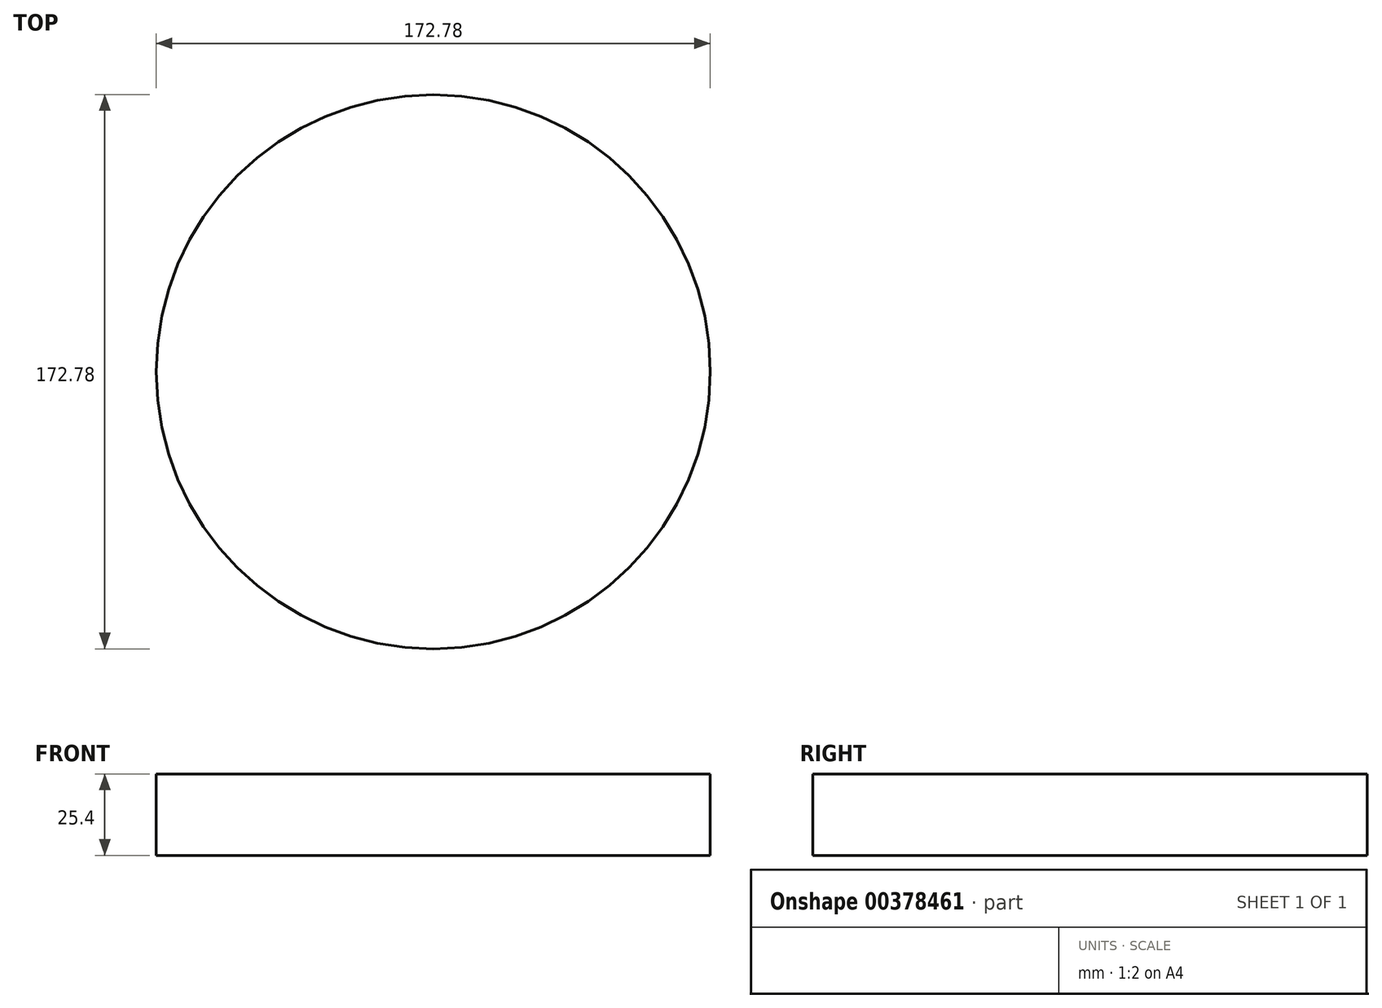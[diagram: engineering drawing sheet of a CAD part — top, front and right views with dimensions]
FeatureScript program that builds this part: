
annotation { "Feature Type Name" : "Feature", "Feature Type Description" : "" }
export const myFeature = defineFeature(function(context is Context, id is Id, definition is map)
    precondition{}
    {
        {
            var Q0;
            Q0=qCreatedBy(makeId("Top.planeOp"),FACE);
            var sketch = newSketch(context, id + "F0", { "sketchPlane" : qUnion([Q0])});
            skCircle(sketch, "E0", {"center": v(0, 0) * mm, "radius": 86.39 * mm});
            skSolve(sketch);
        }
        {
            var Q0;
            Q0=makeQuery(id+"F0.imprint","IMPRINT",FACE,{"disambiguationData":[TD([[makeQuery(id+"F0.imprint","IMPRINT",EDGE,{"derivedFrom":sQuery(id+"F0.wireOp",EDGE,"E0")}),1.0]])]});
            var sketch = newSketch(context, id + "F1", { "sketchPlane" : qUnion([Q0])});
            skCircle(sketch, "E1", {"center": v(0, 0) * mm, "radius": 61.76 * mm});
            skSolve(sketch);
        }
        {
            var Q0;
            Q0=makeQuery(id+"F1.imprint","IMPRINT",FACE,{"disambiguationData":[TD([[makeQuery(id+"F1.imprint","IMPRINT",EDGE,{"derivedFrom":sQuery(id+"F1.wireOp",EDGE,"E1")}),1.0]])]});
            var Q1;
            Q1=makeQuery(id+"F1.imprint","IMPRINT",FACE,{"disambiguationData":[TD([[makeQuery(id+"F1.imprint","IMPRINT",EDGE,{"derivedFrom":sQuery(id+"F1.wireOp",EDGE,"E1")}),-1.0]])]});
            extrude(context, id + "F2", {"entities" : qUnion([Q0, Q1]), "depth" : 25.4 * mm});
        }
    });
